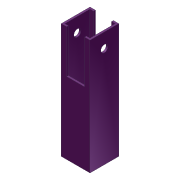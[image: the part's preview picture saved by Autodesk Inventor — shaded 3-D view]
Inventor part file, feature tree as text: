
AUTODESK INVENTOR PART (.ipt)
format: ipt  version: 2012 (Build 160160000, 160)  size: 100,864 bytes
history: native  units: in
note: dims shown in document units (in); Inventor stores cm internally (conversion verified against a paired STEP export)
features: extrude x3, sketch x3, shell x1
ambient origin geometry x8: Origin, YZ Plane, XZ Plane, XY Plane, X Axis, Y Axis, Z Axis, Center Point
bodies: Solid1 (feature_tree)
feature tree (7):
  extrude  "Extrusion1"  Depth=4.0in
  shell  "Shell1"  Thickness=1.0in
  extrude  "Extrusion2"  Depth=0.25in
  extrude  "Extrusion3"  Depth=1.0in TaperAngle=0.0deg
  sketch  "Sketch1"  dims[d0=1.0in d1=4.0in d5=1.0in d6=0.0in]
  sketch  "Sketch2"  dims[d7=0.125in d8=0.25in]
  sketch  "Sketch3"  dims[d9=0.5in d11=1.0in d12=0.0in d13=3.5in d14=1.5in d15=0.1875in d16=0.1875in d17=1.0in d18=0.0in]
